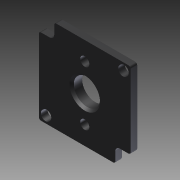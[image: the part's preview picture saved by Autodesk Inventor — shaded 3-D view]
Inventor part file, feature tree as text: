
AUTODESK INVENTOR PART (.ipt)
format: ipt  version: 2014 (Build 180170000, 170)  size: 267,264 bytes
history: native  units: in
note: dims shown in document units (in); Inventor stores cm internally (conversion verified against a paired STEP export)
features: fillet x1, other x1, imported_body x1
ambient origin geometry x8: Origin, YZ Plane, XZ Plane, XY Plane, X Axis, Y Axis, Z Axis, Center Point
bodies: Body1 (feature_tree)
feature tree (3):
  fillet  "Fillet4"  [1 undecoded]
  other  "217-2822-BAG Mounting Plate STEP1"
  imported_body  "Base1"
note: 1 required parameter value undecoded (feature->parameter linkage not recoverable at this tier; creation-order binding heuristic only, values carry confidence <= 0.55)
